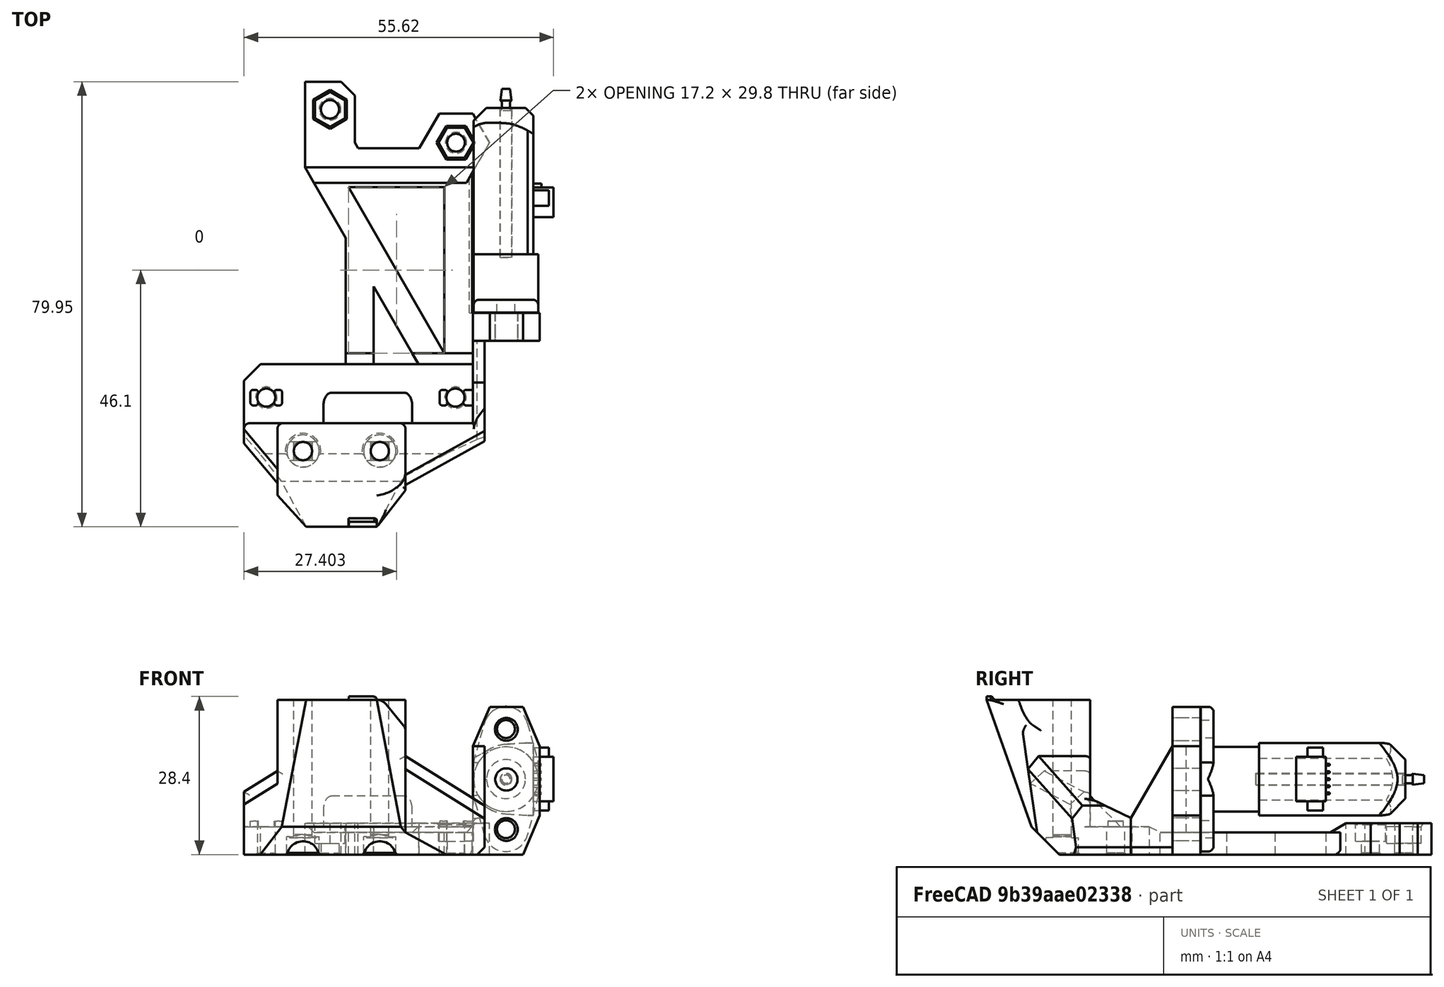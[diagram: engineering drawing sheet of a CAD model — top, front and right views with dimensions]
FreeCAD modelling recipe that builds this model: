
FCSTD DOCUMENT  (FreeCAD 0.18R16146 (Git))
Label: stock-front-bltouch
License: All rights reserved
LicenseURL: http://en.wikipedia.org/wiki/All_rights_reserved
objects: Part::Feature×5, Part::Chamfer×3, Part::Box×2, Part::MultiFuse×2, Mesh::Feature×1
note: 12 computed .brp shape members not serialized (recipe doc carries the construction recipe); baked Part::Feature solids carry a one-line shape summary decoded from their .brp

FEATURE [Part::Feature] Part__Feature023  label="body_front"
  Placement = pos=(-34.475,25.5,59) rot=(0.57735,0.57735,-0.57735;2.0944rad)
  shape: bbox 44.13 x 79.97 x 28.92 mm, 174 faces (baked)
FEATURE [Mesh::Feature] bearmera_bltouch_v4  label="bearmera_bltouch.v4"
  Placement = pos=(-63.3,15.7,20.7) rot=(0,0,1;0rad)
FEATURE [Part::Feature] Cut013027001  label="Cut036009013017007008008021005005044006"
  Placement = pos=(2.175,32,-19) rot=(0,-0.707107,0.707107;3.14159rad)
  shape: bbox 12 x 3 x 26.5 mm, 12 faces (baked)
FEATURE [Part::Feature] Cut013027002  label="Cut036009013017007008008021005005044007"
  Placement = pos=(2.175,30,-19) rot=(0,0.707107,-0.707107;3.14159rad)
  shape: bbox 12 x 3 x 26.5 mm, 12 faces (baked)
FEATURE [Part::Feature] Fusion015  label="bltouch-pref"
  Placement = pos=(28.1,3.6,13.55) rot=(0.57735,-0.57735,0.57735;2.0944rad)
  shape: bbox 16.68 x 40.15 x 26.66 mm, 80 faces (baked)
FEATURE [Part::Box] Box  label="Cube"
  AttacherType = Attacher::AttachEngine3D
  Height = 19.5
  Length = 2.085
  Placement = pos=(22.17,-9,0) rot=(0,0,1;0rad)
  Width = 10
FEATURE [Part::Chamfer] Chamfer
  Base = -> Box
  Edges = 1 edges r=1.3: [Edge8]
FEATURE [Part::Chamfer] Chamfer001
  Base = -> Chamfer
  Edges = 1 edges: [Edge8 r1=13 r2=7.5]
FEATURE [Part::Box] Box001  label="Cube001"
  AttacherType = Attacher::AttachEngine3D
  Height = 4
  Length = 5.25
  Placement = pos=(19,-2.5,0) rot=(0,0,1;0rad)
  Width = 6
FEATURE [Part::Chamfer] Chamfer002
  Base = -> Box001
  Edges = 1 edges r=1.3: [Edge8]
FEATURE [Part::MultiFuse] Fusion
  Shapes = -> [Chamfer002,Cut013027001,Cut013027002,Chamfer001]
FEATURE [Part::MultiFuse] Fusion016
  Shapes = -> [Fusion,Part__Feature023]
FEATURE [Part::Feature] Fusion016001  label="Fusion017"
  shape: bbox 53.17 x 79.97 x 28.92 mm, 192 faces (baked)
